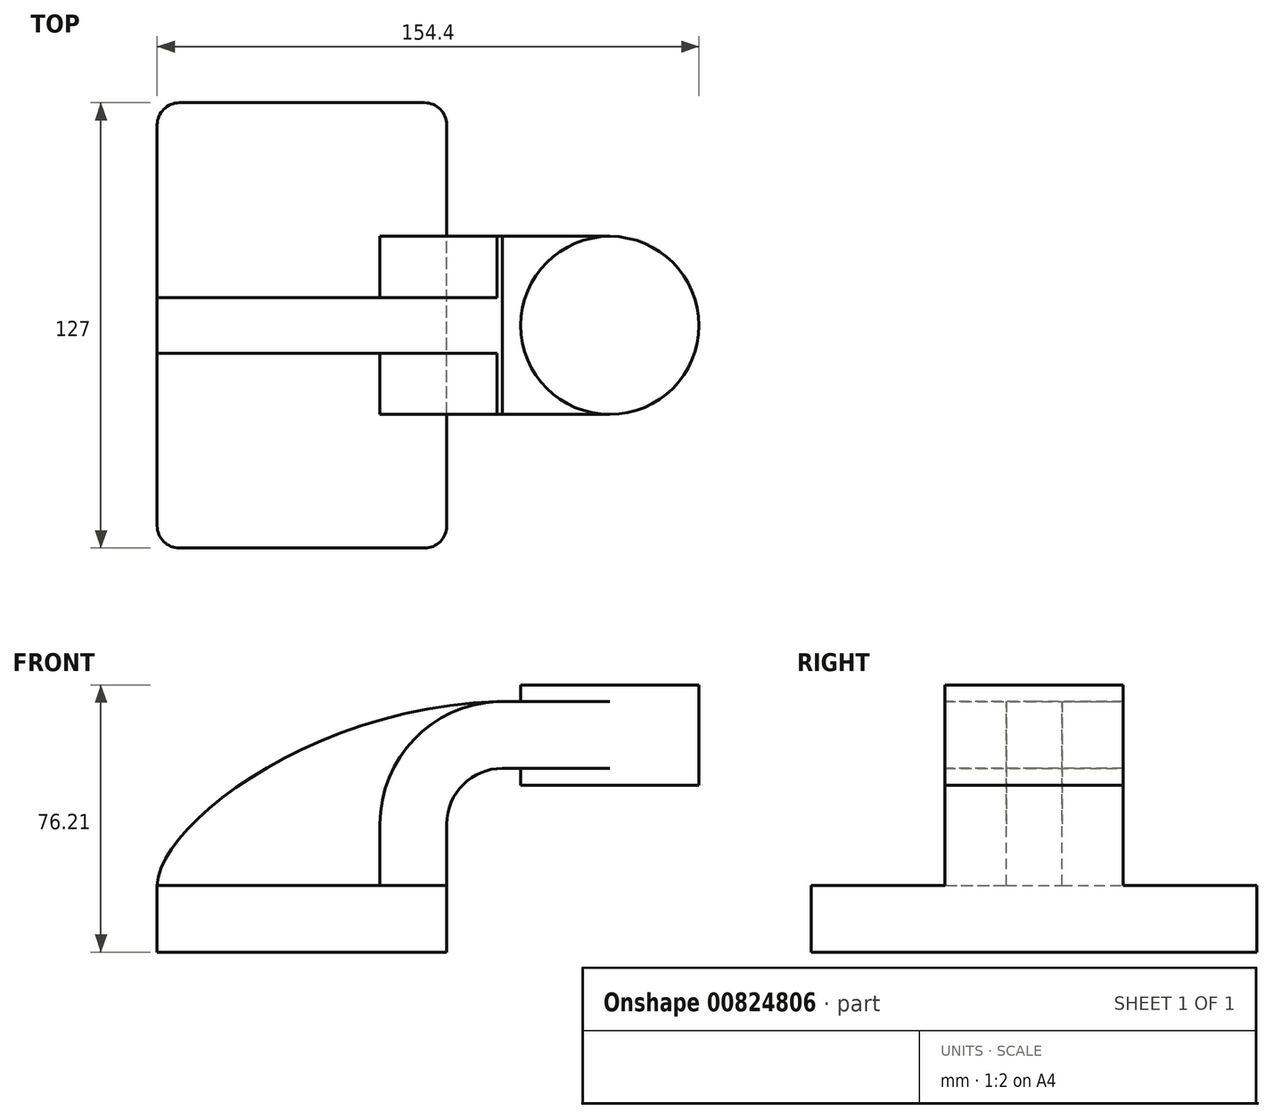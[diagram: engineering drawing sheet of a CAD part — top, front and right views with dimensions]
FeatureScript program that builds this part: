
annotation { "Feature Type Name" : "Feature", "Feature Type Description" : "" }
export const myFeature = defineFeature(function(context is Context, id is Id, definition is map)
    precondition{}
    {
        {
            var Q0;
            Q0=qCreatedBy(makeId("Front.planeOp"),FACE);
            var sketch = newSketch(context, id + "F0", { "sketchPlane" : qUnion([Q0])});
            skLineSegment(sketch, "E0.bottom", {"start": v(-41.28, -9.53) * mm, "end": v(41.28, -9.53) * mm});
            skLineSegment(sketch, "E0.top", {"start": v(-41.28, 9.52) * mm, "end": v(41.27, 9.52) * mm});
            skLineSegment(sketch, "E0.left", {"start": v(-41.27, -9.53) * mm, "end": v(-41.28, 9.52) * mm});
            skLineSegment(sketch, "E0.right", {"start": v(41.28, -9.53) * mm, "end": v(41.27, 9.52) * mm});
            skPoint(sketch, "E0.middle", {"position": v(0, 0) * mm});
            skLineSegment(sketch, "E1.bottom", {"start": v(113.12, 66.67) * mm, "end": v(62.32, 66.67) * mm});
            skLineSegment(sketch, "E1.top", {"start": v(113.12, 38.1) * mm, "end": v(62.32, 38.1) * mm});
            skLineSegment(sketch, "E1.left", {"start": v(113.12, 66.67) * mm, "end": v(113.12, 38.1) * mm});
            skLineSegment(sketch, "E1.right", {"start": v(62.32, 66.67) * mm, "end": v(62.32, 38.1) * mm});
            skPoint(sketch, "E1.middle", {"position": v(87.72, 52.39) * mm});
            skLineSegment(sketch, "E2", {"start": v(41.27, 9.52) * mm, "end": v(41.27, 27) * mm});
            skArc(sketch, "E3", {"start": v(41.27, 27) * mm, "mid": v(45.92, 38.23) * mm, "end": v(57.15, 42.88) * mm});
            skLineSegment(sketch, "E4", {"start": v(57.15, 42.88) * mm, "end": v(87.72, 42.88) * mm});
            skLineSegment(sketch, "E5.0", {"start": v(57.15, 61.93) * mm, "end": v(87.72, 61.93) * mm});
            skArc(sketch, "E5.1", {"start": v(22.22, 27) * mm, "mid": v(32.45, 51.7) * mm, "end": v(57.15, 61.93) * mm});
            skLineSegment(sketch, "E5.2", {"start": v(22.22, 9.52) * mm, "end": v(22.22, 27) * mm});
            skLineSegment(sketch, "E6", {"start": v(87.72, 38.1) * mm, "end": v(87.72, 66.67) * mm});
            skFitSpline(sketch, "E7", {"points": [v(-41.28, 9.53) * mm, v(57.15, 61.93) * mm], "startDerivative": vector(1.76, 52.54) * mm, "endDerivative": vector(159.27, 2.53) * mm});
            skSolve(sketch);
        }
        {
            var Q0;
            Q0=makeQuery(id+"F0.imprint","IMPRINT",FACE,{"disambiguationData":[TD([[makeQuery(id+"F0.imprint","IMPRINT",EDGE,{"derivedFrom":sQuery(id+"F0.wireOp",EDGE,"E0.bottom")}),1.0]])]});
            extrude(context, id + "F1", {"entities" : qUnion([Q0]), "endBound" : BoundingType.SYMMETRIC, "depth" : 127 * mm, "offsetDistance" : 25.4 * mm});
        }
        {
            var Q0;
            {var subQ1=sQuery(id+"F0.wireOp",EDGE,"E2");Q0=makeQuery(id+"F0.imprint","IMPRINT",FACE,{"disambiguationData":[TD([[makeQuery(id+"F0.imprint","IMPRINT",EDGE,{"derivedFrom":subQ1}),1.0]])]});}
            extrude(context, id + "F2", {"entities" : qUnion([Q0]), "operationType" : NewBodyOperationType.ADD, "endBound" : BoundingType.SYMMETRIC, "depth" : 50.8 * mm, "offsetDistance" : 25.4 * mm});
        }
        {
            var Q0;
            {var subQ3=sQuery(id+"F0.wireOp",EDGE,"E5.2");Q0=makeQuery(id+"F0.imprint","IMPRINT",FACE,{"disambiguationData":[TD([[makeQuery(id+"F0.imprint","IMPRINT",EDGE,{"derivedFrom":subQ3}),1.0]])]});}
            extrude(context, id + "F3", {"entities" : qUnion([Q0]), "operationType" : NewBodyOperationType.ADD, "endBound" : BoundingType.SYMMETRIC, "depth" : 15.88 * mm, "offsetDistance" : 25.4 * mm});
        }
        {
            var Q0;
            {var subQ0=sQuery(id+"F0.wireOp",EDGE,"E5.0");var subQ1=sQuery(id+"F0.wireOp",EDGE,"E1.right");var subQ2=makeQuery(id+"F0.imprint","INTERSECT",VERTEX,{"derivedFrom":[subQ1,subQ0]});Q0=makeQuery(id+"F0.imprint","IMPRINT",FACE,{"disambiguationData":[TD([[makeQuery(id+"F0.imprint","IMPRINT",EDGE,{"disambiguationData":[TD([[subQ2,-1.0]])],"derivedFrom":subQ1}),1.0]])]});}
            extrude(context, id + "F4", {"entities" : qUnion([Q0]), "operationType" : NewBodyOperationType.ADD, "endBound" : BoundingType.SYMMETRIC, "depth" : 50.8 * mm, "offsetDistance" : 25.4 * mm});
        }
        {
            var Q0;
            {var subQ0=sQuery(id+"F0.wireOp",EDGE,"E1.left");Q0=makeQuery(id+"F0.imprint","IMPRINT",FACE,{"disambiguationData":[TD([[makeQuery(id+"F0.imprint","IMPRINT",EDGE,{"derivedFrom":subQ0}),-1.0]])]});}
            var Q1;
            Q1=sQuery(id+"F0.wireOp",EDGE,"E6");
            revolve(context, id + "F5", {"operationType" : NewBodyOperationType.ADD, "surfaceOperationType" : NewSurfaceOperationType.NEW, "entities" : qUnion([Q0]), "axis" : qUnion([Q1]), "revolveType" : RevolveType.FULL});
        }
        {
            var Q0;
            Q0=makeQuery(id+"F1.opExtrude","CAP_EDGE",EDGE,{"disambiguationData":[OSD([sQuery(id+"F0.wireOp",EDGE,"E0.right")])],"isStart":true});
            var Q1;
            Q1=makeQuery(id+"F1.opExtrude","CAP_EDGE",EDGE,{"disambiguationData":[OSD([sQuery(id+"F0.wireOp",EDGE,"E0.left")])],"isStart":true});
            var Q2;
            Q2=makeQuery(id+"F1.opExtrude","CAP_EDGE",EDGE,{"disambiguationData":[OSD([sQuery(id+"F0.wireOp",EDGE,"E0.left")])],"isStart":false});
            var Q3;
            Q3=makeQuery(id+"F1.opExtrude","CAP_EDGE",EDGE,{"disambiguationData":[OSD([sQuery(id+"F0.wireOp",EDGE,"E0.right")])],"isStart":false});
            fillet(context, id + "F6", {"entities" : qUnion([Q0, Q1, Q2, Q3]), "radius" : 6.35 * mm, "tangentPropagation" : true, "allowEdgeOverflow" : false});
        }
    });
